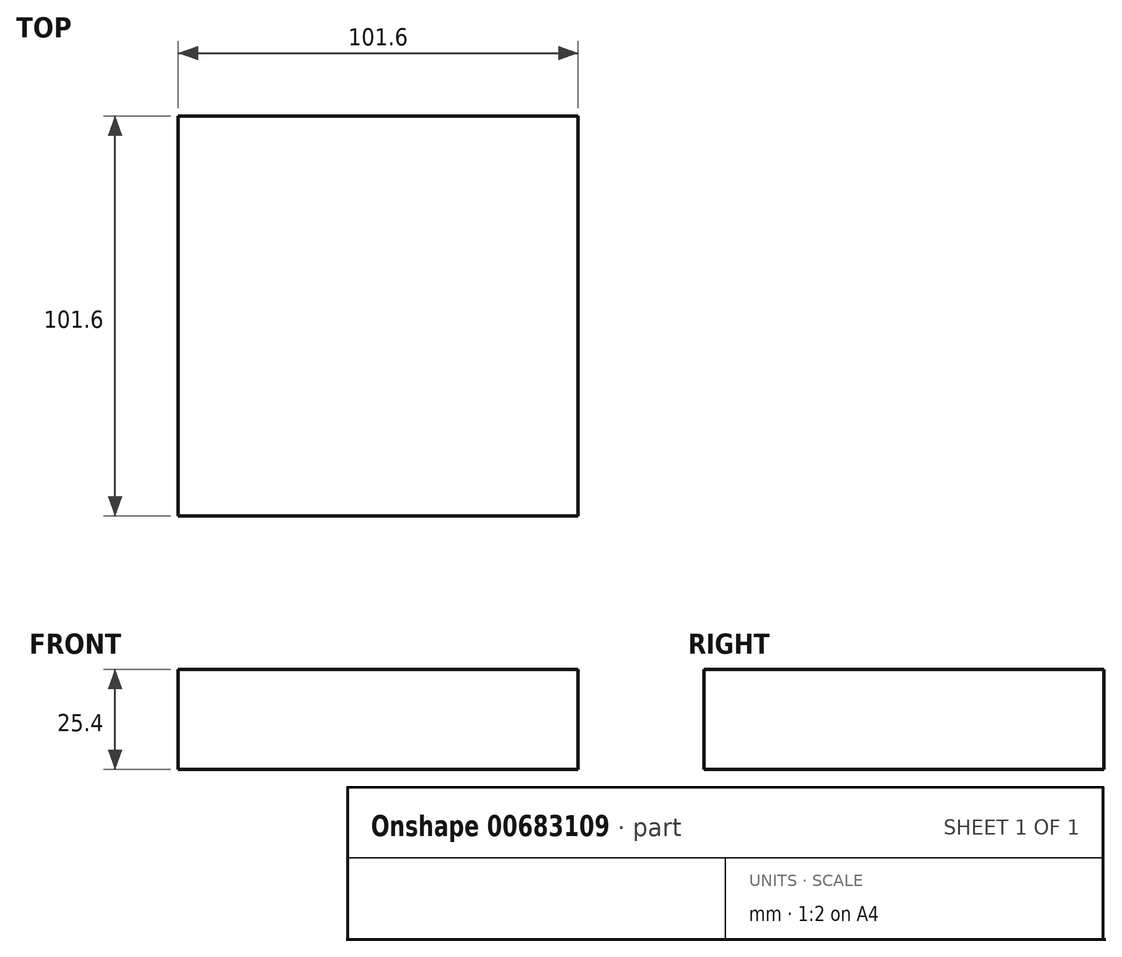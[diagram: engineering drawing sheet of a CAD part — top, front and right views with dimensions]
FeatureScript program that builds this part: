
annotation { "Feature Type Name" : "Feature", "Feature Type Description" : "" }
export const myFeature = defineFeature(function(context is Context, id is Id, definition is map)
    precondition{}
    {
        {
            var Q0;
            Q0=qCreatedBy(makeId("Top.planeOp"),FACE);
            var sketch = newSketch(context, id + "F0", { "sketchPlane" : qUnion([Q0])});
            skLineSegment(sketch, "E0.bottom", {"start": v(50.8, -50.8) * mm, "end": v(-50.8, -50.8) * mm});
            skLineSegment(sketch, "E0.top", {"start": v(50.8, 50.8) * mm, "end": v(-50.8, 50.8) * mm});
            skLineSegment(sketch, "E0.left", {"start": v(50.8, -50.8) * mm, "end": v(50.8, 50.8) * mm});
            skLineSegment(sketch, "E0.right", {"start": v(-50.8, -50.8) * mm, "end": v(-50.8, 50.8) * mm});
            skPoint(sketch, "E0.middle", {"position": v(0, 0) * mm});
            skSolve(sketch);
        }
        {
            var Q0;
            Q0 = qSketchRegion(id + "F0", true);
            extrude(context, id + "F1", {"entities" : qUnion([Q0]), "depth" : 25.4 * mm, "offsetDistance" : 25.4 * mm});
        }
    });
